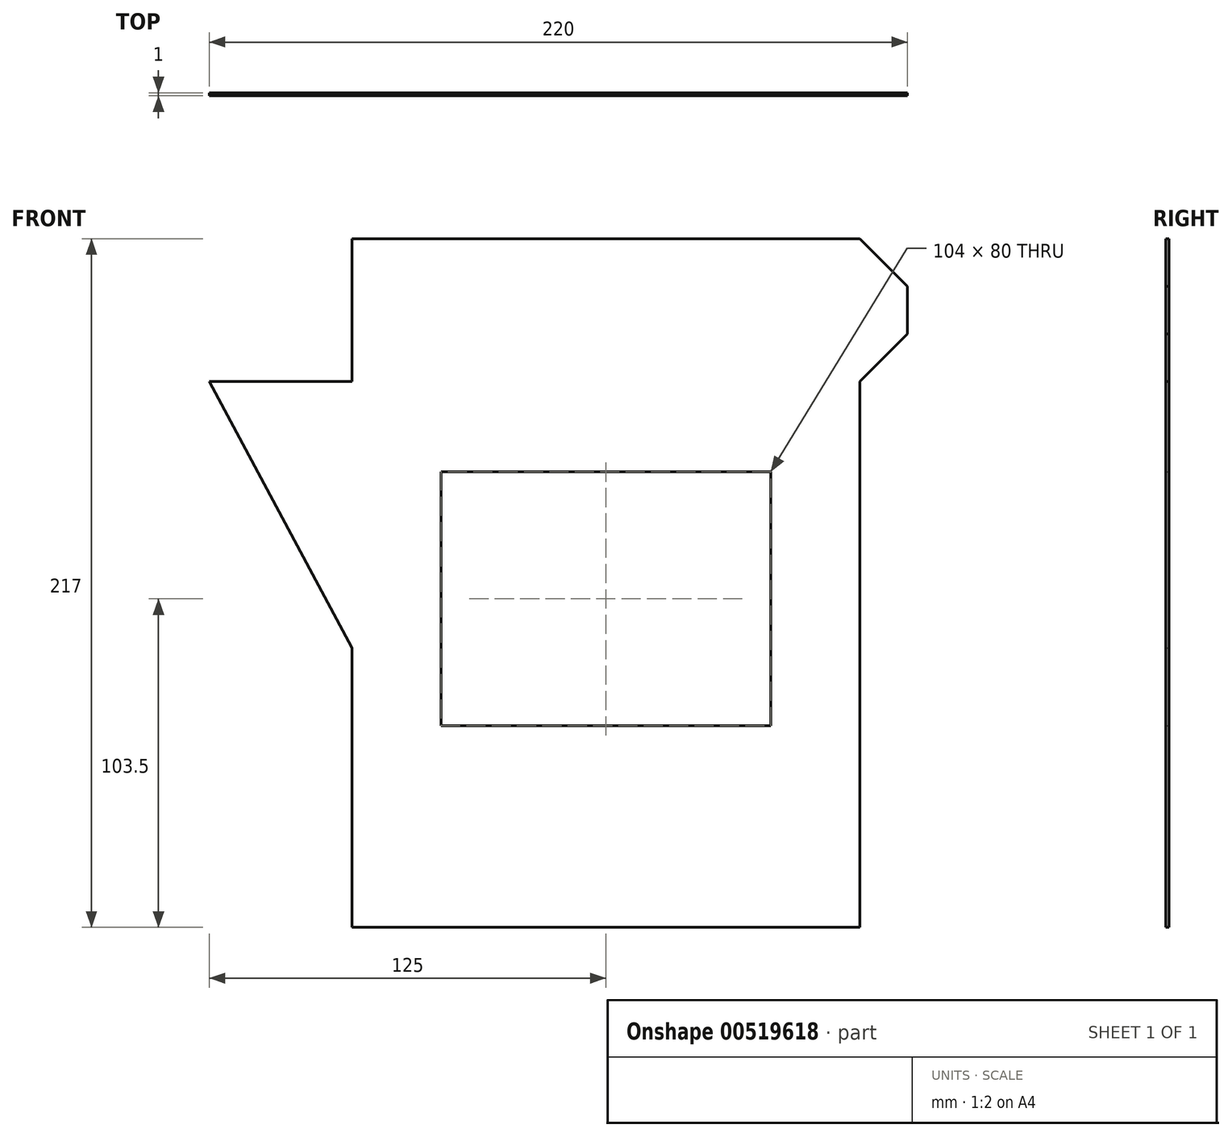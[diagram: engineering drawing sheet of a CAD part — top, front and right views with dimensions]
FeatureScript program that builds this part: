
annotation { "Feature Type Name" : "Feature", "Feature Type Description" : "" }
export const myFeature = defineFeature(function(context is Context, id is Id, definition is map)
    precondition{}
    {
        {
            var Q0;
            Q0=qCreatedBy(makeId("Front.planeOp"),FACE);
            var sketch = newSketch(context, id + "F0", { "sketchPlane" : qUnion([Q0])});
            skLineSegment(sketch, "E0", {"start": v(-125, 86) * mm, "end": v(-80, 2) * mm});
            skLineSegment(sketch, "E1", {"start": v(-80, 2) * mm, "end": v(-80, 86) * mm});
            skLineSegment(sketch, "E2", {"start": v(-80, 86) * mm, "end": v(-125, 86) * mm});
            skLineSegment(sketch, "E3.bottom", {"start": v(80, 86) * mm, "end": v(80, 131) * mm});
            skLineSegment(sketch, "E3.top", {"start": v(-80, 86) * mm, "end": v(-80, 131) * mm});
            skLineSegment(sketch, "E3.left", {"start": v(80, 86) * mm, "end": v(-80, 86) * mm});
            skLineSegment(sketch, "E3.right", {"start": v(80, 131) * mm, "end": v(-80, 131) * mm});
            skPoint(sketch, "E3.middle", {"position": v(0, 108.5) * mm});
            skLineSegment(sketch, "E4.top", {"start": v(80, -86) * mm, "end": v(4.5, -86) * mm});
            skLineSegment(sketch, "E4.left", {"start": v(80, 86) * mm, "end": v(80, -86) * mm});
            skLineSegment(sketch, "E4.right", {"start": v(-80, 86) * mm, "end": v(-80, -86) * mm});
            skPoint(sketch, "E4.middle", {"position": v(0, 0) * mm});
            skLineSegment(sketch, "E5.trimOffspring", {"start": v(-1.5, -86) * mm, "end": v(-80, -86) * mm});
            skLineSegment(sketch, "E6", {"start": v(4.5, -86) * mm, "end": v(-1.5, -86) * mm});
            skLineSegment(sketch, "E7.bottom", {"start": v(52, 57.5) * mm, "end": v(-52, 57.5) * mm});
            skLineSegment(sketch, "E7.top", {"start": v(52, -22.5) * mm, "end": v(-52, -22.5) * mm});
            skLineSegment(sketch, "E7.left", {"start": v(52, 57.5) * mm, "end": v(52, -22.5) * mm});
            skLineSegment(sketch, "E7.right", {"start": v(-52, 57.5) * mm, "end": v(-52, -22.5) * mm});
            skPoint(sketch, "E7.middle", {"position": v(0, 17.5) * mm});
            skLineSegment(sketch, "E8.MirrorCS", {"start": v(80, 2) * mm, "end": v(80, 86) * mm});
            skLineSegment(sketch, "E9.MirrorCS", {"start": v(125, 86) * mm, "end": v(80, 2) * mm});
            skLineSegment(sketch, "E10.MirrorCS", {"start": v(80, 86) * mm, "end": v(125, 86) * mm});
            skLineSegment(sketch, "E11.left", {"start": v(-80, 131) * mm, "end": v(-80, 86) * mm});
            skLineSegment(sketch, "E11.right", {"start": v(-95, 116) * mm, "end": v(-95, 101) * mm});
            skLineSegment(sketch, "E12.top", {"start": v(80, 86) * mm, "end": v(102.5, 86) * mm});
            skLineSegment(sketch, "E12.left", {"start": v(80, 131) * mm, "end": v(80, 86) * mm});
            skLineSegment(sketch, "E13", {"start": v(-80, 131) * mm, "end": v(-95, 116) * mm});
            skLineSegment(sketch, "E14", {"start": v(-80, 86) * mm, "end": v(-95, 101) * mm});
            skLineSegment(sketch, "E15.MirrorCS", {"start": v(95, 116) * mm, "end": v(95, 101) * mm});
            skLineSegment(sketch, "E16.MirrorCS", {"start": v(80, 86) * mm, "end": v(95, 101) * mm});
            skLineSegment(sketch, "E17.MirrorCS", {"start": v(80, 131) * mm, "end": v(95, 116) * mm});
            skSolve(sketch);
        }
        {
            var Q0;
            {var subQ3=sQuery(id+"F0.wireOp",EDGE,"E3.left");Q0=makeQuery(id+"F0.imprint","IMPRINT",FACE,{"disambiguationData":[TD([[makeQuery(id+"F0.imprint","IMPRINT",EDGE,{"derivedFrom":subQ3}),1.0]])]});}
            var Q1;
            Q1=makeQuery(id+"F0.imprint","IMPRINT",FACE,{"disambiguationData":[TD([[makeQuery(id+"F0.imprint","IMPRINT",EDGE,{"derivedFrom":sQuery(id+"F0.wireOp",EDGE,"E8.MirrorCS")}),-1.0]])]});
            var Q2;
            Q2=makeQuery(id+"F0.imprint","IMPRINT",FACE,{"disambiguationData":[TD([[makeQuery(id+"F0.imprint","IMPRINT",EDGE,{"derivedFrom":sQuery(id+"F0.wireOp",EDGE,"E3.right")}),1.0]])]});
            var Q3;
            Q3=makeQuery(id+"F0.imprint","IMPRINT",FACE,{"disambiguationData":[TD([[makeQuery(id+"F0.imprint","IMPRINT",EDGE,{"derivedFrom":sQuery(id+"F0.wireOp",EDGE,"E11.left")}),-1.0]])]});
            var Q4;
            {var subQ0=sQuery(id+"F0.wireOp",EDGE,"E0");Q4=makeQuery(id+"F0.imprint","IMPRINT",FACE,{"disambiguationData":[TD([[makeQuery(id+"F0.imprint","IMPRINT",EDGE,{"derivedFrom":subQ0}),1.0]])]});}
            var Q5;
            Q5=makeQuery(id+"F0.imprint","IMPRINT",FACE,{"disambiguationData":[TD([[makeQuery(id+"F0.imprint","IMPRINT",EDGE,{"derivedFrom":sQuery(id+"F0.wireOp",EDGE,"E15.MirrorCS")}),-1.0]])]});
            extrude(context, id + "F1", {"entities" : qUnion([Q0, Q1, Q2, Q3, Q4, Q5]), "depth" : 1 * mm, "offsetDistance" : 25 * mm});
        }
    });
